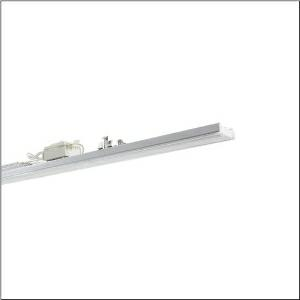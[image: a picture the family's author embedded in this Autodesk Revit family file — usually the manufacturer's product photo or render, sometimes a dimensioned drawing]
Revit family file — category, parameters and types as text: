
# Revit family: licross_r__11_recessed_mo_51tl10de445g_6e9c
name_source: partatom
category: Lighting Fixtures
units: mm (PartAtom-declared; Revit-internal decimal feet)

## family parameters
Cut with Voids When Loaded = No
Host = Face
Light Source = No
Part Type = Normal
Room Calculation Point = No
Round Connector Dimension = Use Diameter
Shared = No

## types (1)
- --- (1 x LED, 4980 lm, 29.6 W, 4000K)
    Apparent Load = 30 VA
    CIE Flux Codes = 50 81 96 100 100
    Color Rendering = 80
    Color Temperature = 4000K
    Default Elevation = 1800 mm
    Description = Licross® 11 Recessed MO, luminaire insert, of sheet steel, coil coated, white, length: 750mm, width: 66mm, height: 67mm, LED rated luminous flux: 4.980lm, light colour: 840, control gear: DALI 2, with plug, 5-pole, with phase selection, mains connection: 220..240V, AC, 50/60Hz, rated input power: 30W, halogen-free wiring, primary optical cover: cover, of PMMA, light emission: direct distribution, primary light characteristic: symmetric, protection rating (complete): IP40, insulation class (complete): insulation class I (protective earthing), certification: CE, ENEC, VDE, UKCA, protection symbol: D if used in an environment without relevant dust loads with corresponding accessories, impact resistance: IK06, permissible ambient temperature for indoor applications: -25..+35°C, corresponds to IFS (International Featured Standards) requirements for safety and quality in the food industry, reducing of maximum allowable ambient temperature of 5°C with ceiling mounting, LABS conformity tested according to VDMA 24364:2018-05, packaging unit: 1 piece
    Height = 58 mm
    Lamp = 1 x LED
    Lamp Light Flux = 4980 lm
    Lamp Power = 29.6 W
    Lamp count = 1
    Length = 750 mm
    Luminous efficacy = 168 lm/W
    Manufacturer = Siteco
    ModVariant = No
    Model = 51TL10DE445G
    Mounting Place = Ceiling
    Mounting Type = Pendant
    Number of Poles = 1
    OnlyDefault = Yes
    Power Factor = 1
    Product Name = Licross® 11 Recessed MO
    Product group = luminaire insert
    ProductGroupID = 902
    Protection Class = Protection class I
    Protection Degree = IP 40
    RLX_Detail_Level = 1
    RLX_Emergency_Light_Flux = 0 lm
    RLX_Emergency_Type = 0
    RLX_Emergency_Type_DB = No
    RlxData = <blob elided: 28985 chars, md5=c49957d2>
    Socket = socket
    Standby Power = 0 W
    System Light Flux = 4980 lm
    System Power = 30 W
    Type Comments = factory setting: luminous flux: 100 % | dim-lin: 254 | 378 mA
    Type Image = l_1296930.jpg
    URL = http://relux.com
    VarID = @adj_099734
    Voltage = 0 V
    Weight = 0.00 kg
    Width = 66 mm

## geometry (parser evidence)
native form markers: Blend x4, Sweep x9
no freeform markers — native parametric forms only
